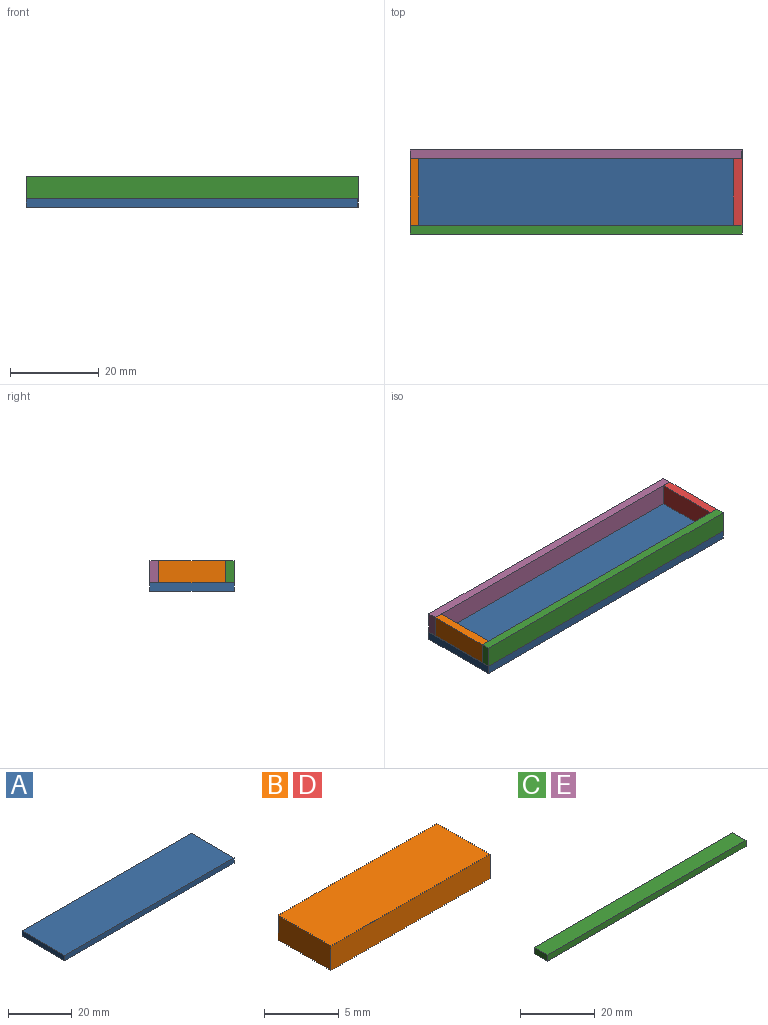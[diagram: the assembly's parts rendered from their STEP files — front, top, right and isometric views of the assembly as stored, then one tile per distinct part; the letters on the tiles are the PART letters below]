
ASSEMBLY  parts=5 mates=5
PART A: 6 faces, bbox 75x19x2 mm
  f0: plane 75x2mm, normal (0,-1,0), area 150mm2, adj f1,f3,f4,f5
  f1: plane 19x2mm, normal (1,0,0), area 38mm2, adj f0,f2,f4,f5
  f2: plane 75x2mm, normal (0,1,0), area 150mm2, adj f1,f3,f4,f5
  f3: plane 19x2mm, normal (-1,0,0), area 38mm2, adj f0,f2,f4,f5
  f4: plane 75x19mm, normal (0,0,1), area 1425mm2, adj f0,f1,f2,f3
  f5: plane 75x19mm, normal (0,0,-1), area 1425mm2, adj f0,f1,f2,f3
PART B: 6 faces, bbox 15x5x2 mm
  f0: plane 15x2mm, normal (0,-1,0), area 30mm2, adj f1,f3,f4,f5
  f1: plane 5x2mm, normal (1,0,0), area 10mm2, adj f0,f2,f4,f5
  f2: plane 15x2mm, normal (0,1,0), area 30mm2, adj f1,f3,f4,f5
  f3: plane 5x2mm, normal (-1,0,0), area 10mm2, adj f0,f2,f4,f5
  f4: plane 15x5mm, normal (0,0,1), area 75mm2, adj f0,f1,f2,f3
  f5: plane 15x5mm, normal (0,0,-1), area 75mm2, adj f0,f1,f2,f3
PART C: 6 faces, bbox 75x5x2 mm
  f0: plane 75x2mm, normal (0,-1,0), area 150mm2, adj f1,f3,f4,f5
  f1: plane 5x2mm, normal (1,0,0), area 10mm2, adj f0,f2,f4,f5
  f2: plane 75x2mm, normal (0,1,0), area 150mm2, adj f1,f3,f4,f5
  f3: plane 5x2mm, normal (-1,0,0), area 10mm2, adj f0,f2,f4,f5
  f4: plane 75x5mm, normal (0,0,1), area 375mm2, adj f0,f1,f2,f3
  f5: plane 75x5mm, normal (0,0,-1), area 375mm2, adj f0,f1,f2,f3
PART D: same geometry as B
PART E: same geometry as C
PLACE A t=(50.9,4.85,16.74)mm
PLACE B rot(axis=(-0.58,0.58,-0.58),120deg) t=(-24.1,6.85,23.74)mm
PLACE C rot(axis=(-1,0,0),90deg) t=(50.9,4.85,23.74)mm
PLACE D rot(axis=(-0.58,-0.58,0.58),120deg) t=(50.9,21.85,23.74)mm
PLACE E rot(axis=(1,0,0),90deg) t=(50.9,23.85,18.74)mm
MATE fastened E.f4 <-> B.f3  axis (0,-1,0) through (-24.1,21.85,21.24)mm
MATE fastened A.f4 <-> D.f2  axis (0,0,1) through (50.9,14.35,18.74)mm
MATE fastened D.f5 <-> E.f1  axis (1,0,0) through (50.9,21.85,21.24)mm
MATE fastened C.f4 <-> B.f1  axis (0,1,0) through (-24.1,6.85,21.24)mm
MATE fastened D.f5 <-> C.f1  axis (1,0,0) through (50.9,6.85,21.24)mm
